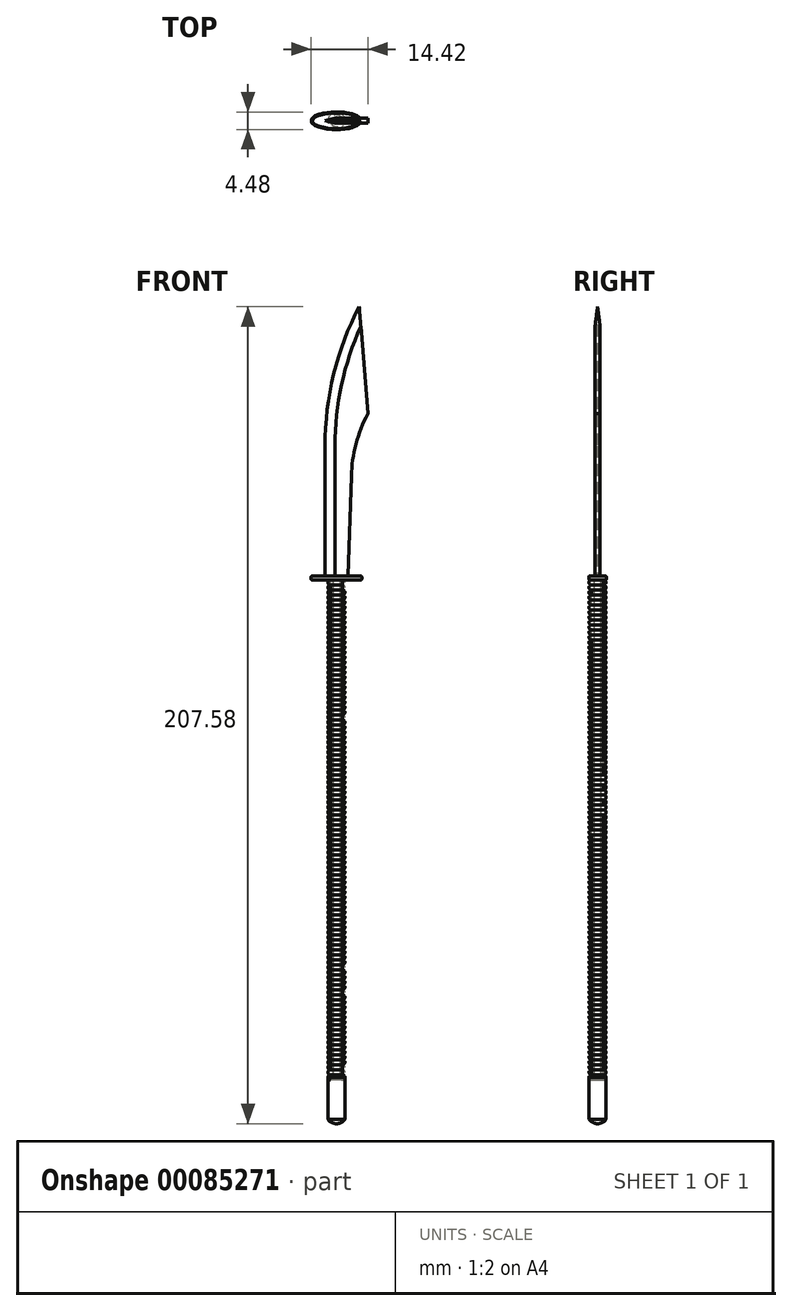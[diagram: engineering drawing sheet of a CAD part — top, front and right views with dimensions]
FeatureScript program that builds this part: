
annotation { "Feature Type Name" : "Feature", "Feature Type Description" : "" }
export const myFeature = defineFeature(function(context is Context, id is Id, definition is map)
    precondition{}
    {
        {
            var Q0;
            Q0=qCreatedBy(makeId("Right.planeOp"),FACE);
            var sketch = newSketch(context, id + "F0", { "sketchPlane" : qUnion([Q0])});
            skLineSegment(sketch, "E0", {"start": v(0, 0) * mm, "end": v(0, -127) * mm});
            skLineSegment(sketch, "E1", {"start": v(0, 0) * mm, "end": v(-1.52, 0) * mm});
            skLineSegment(sketch, "E2", {"start": v(-1.52, 0) * mm, "end": v(-1.52, -127) * mm});
            skLineSegment(sketch, "E3", {"start": v(0, -127) * mm, "end": v(-1.52, -127) * mm});
            skSolve(sketch);
        }
        {
            var Q0;
            Q0 = qSketchRegion(id + "F0", true);
            var Q1;
            Q1=sQuery(id+"F0.wireOp",EDGE,"E0");
            revolve(context, id + "F1", {"entities" : qUnion([Q0]), "axis" : qUnion([Q1]), "revolveType" : RevolveType.FULL});
        }
        {
            var Q0;
            Q0=qCreatedBy(makeId("Right.planeOp"),FACE);
            var sketch = newSketch(context, id + "F2", { "sketchPlane" : qUnion([Q0])});
            skLineSegment(sketch, "E4", {"start": v(-1.52, -127) * mm, "end": v(-1.52, 0) * mm});
            skCircle(sketch, "E5", {"center": v(-1.52, -0.63) * mm, "radius": 0.64 * mm});
            skCircle(sketch, "E6.1.0.0", {"center": v(-1.52, -1.9) * mm, "radius": 0.64 * mm});
            skCircle(sketch, "E6.2.0.0", {"center": v(-1.52, -3.17) * mm, "radius": 0.64 * mm});
            skCircle(sketch, "E6.3.0.0", {"center": v(-1.52, -4.44) * mm, "radius": 0.64 * mm});
            skCircle(sketch, "E6.4.0.0", {"center": v(-1.52, -5.71) * mm, "radius": 0.64 * mm});
            skCircle(sketch, "E6.5.0.0", {"center": v(-1.52, -6.98) * mm, "radius": 0.64 * mm});
            skCircle(sketch, "E6.6.0.0", {"center": v(-1.52, -8.25) * mm, "radius": 0.64 * mm});
            skCircle(sketch, "E6.7.0.0", {"center": v(-1.52, -9.52) * mm, "radius": 0.64 * mm});
            skCircle(sketch, "E6.8.0.0", {"center": v(-1.52, -10.8) * mm, "radius": 0.64 * mm});
            skCircle(sketch, "E6.9.0.0", {"center": v(-1.52, -12.06) * mm, "radius": 0.64 * mm});
            skCircle(sketch, "E6.10.0.0", {"center": v(-1.52, -13.33) * mm, "radius": 0.64 * mm});
            skCircle(sketch, "E6.11.0.0", {"center": v(-1.52, -14.6) * mm, "radius": 0.64 * mm});
            skCircle(sketch, "E6.12.0.0", {"center": v(-1.52, -15.88) * mm, "radius": 0.64 * mm});
            skCircle(sketch, "E6.13.0.0", {"center": v(-1.52, -17.14) * mm, "radius": 0.64 * mm});
            skCircle(sketch, "E6.14.0.0", {"center": v(-1.52, -18.41) * mm, "radius": 0.64 * mm});
            skCircle(sketch, "E6.15.0.0", {"center": v(-1.52, -19.69) * mm, "radius": 0.64 * mm});
            skCircle(sketch, "E6.16.0.0", {"center": v(-1.52, -20.96) * mm, "radius": 0.64 * mm});
            skCircle(sketch, "E6.17.0.0", {"center": v(-1.52, -22.23) * mm, "radius": 0.64 * mm});
            skCircle(sketch, "E6.18.0.0", {"center": v(-1.52, -23.5) * mm, "radius": 0.64 * mm});
            skCircle(sketch, "E6.19.0.0", {"center": v(-1.52, -24.77) * mm, "radius": 0.64 * mm});
            skCircle(sketch, "E6.20.0.0", {"center": v(-1.52, -26.04) * mm, "radius": 0.64 * mm});
            skCircle(sketch, "E6.21.0.0", {"center": v(-1.52, -27.3) * mm, "radius": 0.64 * mm});
            skCircle(sketch, "E6.22.0.0", {"center": v(-1.52, -28.58) * mm, "radius": 0.64 * mm});
            skCircle(sketch, "E6.23.0.0", {"center": v(-1.52, -29.85) * mm, "radius": 0.64 * mm});
            skCircle(sketch, "E6.24.0.0", {"center": v(-1.52, -31.12) * mm, "radius": 0.64 * mm});
            skCircle(sketch, "E6.25.0.0", {"center": v(-1.52, -32.39) * mm, "radius": 0.64 * mm});
            skCircle(sketch, "E6.26.0.0", {"center": v(-1.52, -33.66) * mm, "radius": 0.64 * mm});
            skCircle(sketch, "E6.27.0.0", {"center": v(-1.52, -34.93) * mm, "radius": 0.64 * mm});
            skCircle(sketch, "E6.28.0.0", {"center": v(-1.52, -36.2) * mm, "radius": 0.64 * mm});
            skCircle(sketch, "E6.29.0.0", {"center": v(-1.52, -37.47) * mm, "radius": 0.64 * mm});
            skCircle(sketch, "E6.30.0.0", {"center": v(-1.52, -38.74) * mm, "radius": 0.64 * mm});
            skCircle(sketch, "E6.31.0.0", {"center": v(-1.52, -40) * mm, "radius": 0.64 * mm});
            skCircle(sketch, "E6.32.0.0", {"center": v(-1.52, -41.28) * mm, "radius": 0.64 * mm});
            skCircle(sketch, "E6.33.0.0", {"center": v(-1.52, -42.55) * mm, "radius": 0.64 * mm});
            skCircle(sketch, "E6.34.0.0", {"center": v(-1.52, -43.82) * mm, "radius": 0.64 * mm});
            skCircle(sketch, "E6.35.0.0", {"center": v(-1.52, -45.09) * mm, "radius": 0.64 * mm});
            skCircle(sketch, "E6.36.0.0", {"center": v(-1.52, -46.36) * mm, "radius": 0.64 * mm});
            skCircle(sketch, "E6.37.0.0", {"center": v(-1.52, -47.63) * mm, "radius": 0.64 * mm});
            skCircle(sketch, "E6.38.0.0", {"center": v(-1.52, -48.9) * mm, "radius": 0.64 * mm});
            skCircle(sketch, "E6.39.0.0", {"center": v(-1.52, -50.17) * mm, "radius": 0.64 * mm});
            skCircle(sketch, "E6.40.0.0", {"center": v(-1.52, -51.44) * mm, "radius": 0.64 * mm});
            skCircle(sketch, "E6.41.0.0", {"center": v(-1.52, -52.7) * mm, "radius": 0.64 * mm});
            skCircle(sketch, "E6.42.0.0", {"center": v(-1.52, -53.98) * mm, "radius": 0.64 * mm});
            skCircle(sketch, "E6.43.0.0", {"center": v(-1.52, -55.25) * mm, "radius": 0.64 * mm});
            skCircle(sketch, "E6.44.0.0", {"center": v(-1.52, -56.52) * mm, "radius": 0.64 * mm});
            skCircle(sketch, "E6.45.0.0", {"center": v(-1.52, -57.79) * mm, "radius": 0.64 * mm});
            skCircle(sketch, "E6.46.0.0", {"center": v(-1.52, -59.06) * mm, "radius": 0.64 * mm});
            skCircle(sketch, "E6.47.0.0", {"center": v(-1.52, -60.33) * mm, "radius": 0.64 * mm});
            skCircle(sketch, "E6.48.0.0", {"center": v(-1.52, -61.6) * mm, "radius": 0.64 * mm});
            skCircle(sketch, "E6.49.0.0", {"center": v(-1.52, -62.87) * mm, "radius": 0.64 * mm});
            skCircle(sketch, "E6.50.0.0", {"center": v(-1.52, -64.14) * mm, "radius": 0.64 * mm});
            skCircle(sketch, "E6.51.0.0", {"center": v(-1.52, -65.4) * mm, "radius": 0.64 * mm});
            skCircle(sketch, "E6.52.0.0", {"center": v(-1.52, -66.68) * mm, "radius": 0.64 * mm});
            skCircle(sketch, "E6.53.0.0", {"center": v(-1.52, -67.95) * mm, "radius": 0.64 * mm});
            skCircle(sketch, "E6.54.0.0", {"center": v(-1.52, -69.22) * mm, "radius": 0.64 * mm});
            skCircle(sketch, "E6.55.0.0", {"center": v(-1.52, -70.49) * mm, "radius": 0.64 * mm});
            skCircle(sketch, "E6.56.0.0", {"center": v(-1.52, -71.76) * mm, "radius": 0.64 * mm});
            skCircle(sketch, "E6.57.0.0", {"center": v(-1.52, -73.03) * mm, "radius": 0.64 * mm});
            skCircle(sketch, "E6.58.0.0", {"center": v(-1.52, -74.3) * mm, "radius": 0.64 * mm});
            skCircle(sketch, "E6.59.0.0", {"center": v(-1.52, -75.57) * mm, "radius": 0.64 * mm});
            skCircle(sketch, "E6.60.0.0", {"center": v(-1.52, -76.84) * mm, "radius": 0.64 * mm});
            skCircle(sketch, "E6.61.0.0", {"center": v(-1.52, -78.1) * mm, "radius": 0.64 * mm});
            skCircle(sketch, "E6.62.0.0", {"center": v(-1.52, -79.38) * mm, "radius": 0.64 * mm});
            skCircle(sketch, "E6.63.0.0", {"center": v(-1.52, -80.65) * mm, "radius": 0.64 * mm});
            skCircle(sketch, "E6.64.0.0", {"center": v(-1.52, -81.92) * mm, "radius": 0.64 * mm});
            skCircle(sketch, "E6.65.0.0", {"center": v(-1.52, -83.19) * mm, "radius": 0.64 * mm});
            skCircle(sketch, "E6.66.0.0", {"center": v(-1.52, -84.46) * mm, "radius": 0.64 * mm});
            skCircle(sketch, "E6.67.0.0", {"center": v(-1.52, -85.73) * mm, "radius": 0.64 * mm});
            skCircle(sketch, "E6.68.0.0", {"center": v(-1.52, -87) * mm, "radius": 0.64 * mm});
            skCircle(sketch, "E6.69.0.0", {"center": v(-1.52, -88.27) * mm, "radius": 0.64 * mm});
            skCircle(sketch, "E6.70.0.0", {"center": v(-1.52, -89.54) * mm, "radius": 0.64 * mm});
            skCircle(sketch, "E6.71.0.0", {"center": v(-1.52, -90.8) * mm, "radius": 0.64 * mm});
            skCircle(sketch, "E6.72.0.0", {"center": v(-1.52, -92.08) * mm, "radius": 0.64 * mm});
            skCircle(sketch, "E6.73.0.0", {"center": v(-1.52, -93.35) * mm, "radius": 0.64 * mm});
            skCircle(sketch, "E6.74.0.0", {"center": v(-1.52, -94.62) * mm, "radius": 0.64 * mm});
            skCircle(sketch, "E6.75.0.0", {"center": v(-1.52, -95.89) * mm, "radius": 0.64 * mm});
            skCircle(sketch, "E6.76.0.0", {"center": v(-1.52, -97.16) * mm, "radius": 0.64 * mm});
            skCircle(sketch, "E6.77.0.0", {"center": v(-1.52, -98.43) * mm, "radius": 0.64 * mm});
            skCircle(sketch, "E6.78.0.0", {"center": v(-1.52, -99.7) * mm, "radius": 0.64 * mm});
            skCircle(sketch, "E6.79.0.0", {"center": v(-1.52, -100.97) * mm, "radius": 0.64 * mm});
            skCircle(sketch, "E6.80.0.0", {"center": v(-1.52, -102.24) * mm, "radius": 0.64 * mm});
            skCircle(sketch, "E6.81.0.0", {"center": v(-1.52, -103.5) * mm, "radius": 0.64 * mm});
            skCircle(sketch, "E6.82.0.0", {"center": v(-1.52, -104.78) * mm, "radius": 0.64 * mm});
            skCircle(sketch, "E6.83.0.0", {"center": v(-1.52, -106.05) * mm, "radius": 0.64 * mm});
            skCircle(sketch, "E6.84.0.0", {"center": v(-1.52, -107.32) * mm, "radius": 0.64 * mm});
            skCircle(sketch, "E6.85.0.0", {"center": v(-1.52, -108.59) * mm, "radius": 0.64 * mm});
            skCircle(sketch, "E6.86.0.0", {"center": v(-1.52, -109.86) * mm, "radius": 0.64 * mm});
            skCircle(sketch, "E6.87.0.0", {"center": v(-1.52, -111.13) * mm, "radius": 0.64 * mm});
            skCircle(sketch, "E6.88.0.0", {"center": v(-1.52, -112.4) * mm, "radius": 0.64 * mm});
            skCircle(sketch, "E6.89.0.0", {"center": v(-1.52, -113.67) * mm, "radius": 0.64 * mm});
            skCircle(sketch, "E6.90.0.0", {"center": v(-1.52, -114.94) * mm, "radius": 0.64 * mm});
            skCircle(sketch, "E6.91.0.0", {"center": v(-1.52, -116.2) * mm, "radius": 0.64 * mm});
            skCircle(sketch, "E6.92.0.0", {"center": v(-1.52, -117.48) * mm, "radius": 0.64 * mm});
            skCircle(sketch, "E6.93.0.0", {"center": v(-1.52, -118.75) * mm, "radius": 0.64 * mm});
            skCircle(sketch, "E6.94.0.0", {"center": v(-1.52, -120.02) * mm, "radius": 0.64 * mm});
            skCircle(sketch, "E6.95.0.0", {"center": v(-1.52, -121.29) * mm, "radius": 0.64 * mm});
            skCircle(sketch, "E6.96.0.0", {"center": v(-1.52, -122.56) * mm, "radius": 0.64 * mm});
            skCircle(sketch, "E6.97.0.0", {"center": v(-1.52, -123.83) * mm, "radius": 0.64 * mm});
            skCircle(sketch, "E6.98.0.0", {"center": v(-1.52, -125.1) * mm, "radius": 0.64 * mm});
            skCircle(sketch, "E6.99.0.0", {"center": v(-1.52, -126.37) * mm, "radius": 0.64 * mm});
            skLineSegment(sketch, "E6.direction1", {"start": v(-1.52, -0.63) * mm, "end": v(-1.52, -1.9) * mm, "construction": true});
            skLineSegment(sketch, "E7", {"start": v(0, 0) * mm, "end": v(0, -126.88) * mm});
            skLineSegment(sketch, "E8", {"start": v(0, -126.88) * mm, "end": v(15.16, -117.8) * mm});
            skSolve(sketch);
        }
        {
            var Q0;
            Q0 = qSketchRegion(id + "F2", true);
            var Q1;
            Q1=sQuery(id+"F2.wireOp",EDGE,"E7");
            revolve(context, id + "F3", {"entities" : qUnion([Q0]), "axis" : qUnion([Q1]), "revolveType" : RevolveType.FULL});
        }
        {
            var Q0;
            Q0=makeQuery(id+"F1.opRevolve","SWEPT_FACE",FACE,{"disambiguationData":[OSD([sQuery(id+"F0.wireOp",EDGE,"E1")])]});
            var sketch = newSketch(context, id + "F4", { "sketchPlane" : qUnion([Q0])});
            skPoint(sketch, "E9", {"position": v(0, -2.24) * mm});
            skPoint(sketch, "E10", {"position": v(0, 2.24) * mm});
            skEllipse(sketch, "E11", {"center": v(0, 0) * mm, "majorRadius": 2.24 * mm, "minorRadius": 6.44 * mm, "majorAxis": v(0, -1)});
            skLineSegment(sketch, "E12", {"start": v(6.44, 0) * mm, "end": v(-6.44, 0) * mm});
            skSolve(sketch);
        }
        {
            var Q0;
            Q0 = qSketchRegion(id + "F4", true);
            extrude(context, id + "F5", {"entities" : qUnion([Q0]), "depth" : 1.02 * mm});
        }
        {
            var Q0;
            Q0=makeQuery(id+"F5.opExtrude","CAP_EDGE",EDGE,{"disambiguationData":[OSD([sQuery(id+"F4.wireOp",EDGE,"E11")])],"isStart":false});
            var Q1;
            Q1=makeQuery(id+"F5.opExtrude","CAP_EDGE",EDGE,{"disambiguationData":[OSD([sQuery(id+"F4.wireOp",EDGE,"E11")])],"isStart":true});
            fillet(context, id + "F6", {"entities" : qUnion([Q0, Q1]), "radius" : 0.25 * mm, "tangentPropagation" : true, "allowEdgeOverflow" : false});
        }
        {
            var Q0;
            Q0=qCreatedBy(makeId("Front.planeOp"),FACE);
            var sketch = newSketch(context, id + "F7", { "sketchPlane" : qUnion([Q0])});
            skLineSegment(sketch, "E13.0", {"start": v(6.44, 0) * mm, "end": v(-6.44, 0) * mm});
            skLineSegment(sketch, "E14.top", {"start": v(6.44, 1.02) * mm, "end": v(-6.44, 1.02) * mm});
            skLineSegment(sketch, "E14.left", {"start": v(6.44, 0) * mm, "end": v(6.44, 1.02) * mm});
            skLineSegment(sketch, "E14.right", {"start": v(-6.44, 0) * mm, "end": v(-6.44, 1.02) * mm});
            skPoint(sketch, "E15", {"position": v(2.88, 1.02) * mm});
            skPoint(sketch, "E16", {"position": v(-2.88, 1.02) * mm});
            skLineSegment(sketch, "E17", {"start": v(2.88, 1.02) * mm, "end": v(3.77, 26.4) * mm});
            skLineSegment(sketch, "E18", {"start": v(-2.88, 1.02) * mm, "end": v(-2.88, 34.04) * mm});
            skArc(sketch, "E19", {"start": v(5.78, 69.43) * mm, "mid": v(-0.69, 52.26) * mm, "end": v(-2.88, 34.04) * mm});
            skArc(sketch, "E20", {"start": v(7.98, 42.21) * mm, "mid": v(4.98, 34.54) * mm, "end": v(3.77, 26.4) * mm});
            skLineSegment(sketch, "E21", {"start": v(7.98, 42.21) * mm, "end": v(5.78, 69.43) * mm});
            skSolve(sketch);
        }
        {
            var Q0;
            {var subQ0=sQuery(id+"F7.wireOp",EDGE,"E17");Q0=makeQuery(id+"F7.imprint","IMPRINT",FACE,{"disambiguationData":[TD([[makeQuery(id+"F7.imprint","IMPRINT",EDGE,{"derivedFrom":subQ0}),1.0]])]});}
            extrude(context, id + "F8", {"entities" : qUnion([Q0]), "endBound" : BoundingType.SYMMETRIC, "depth" : 1.27 * mm});
        }
        {
            var Q0;
            Q0=makeQuery(id+"F8.opExtrude","CAP_EDGE",EDGE,{"disambiguationData":[OSD([sQuery(id+"F7.wireOp",EDGE,"E19")])],"isStart":true});
            var Q1;
            Q1=makeQuery(id+"F8.opExtrude","CAP_EDGE",EDGE,{"disambiguationData":[OSD([sQuery(id+"F7.wireOp",EDGE,"E18")])],"isStart":true});
            var Q2;
            Q2=makeQuery(id+"F8.opExtrude","CAP_EDGE",EDGE,{"disambiguationData":[OSD([sQuery(id+"F7.wireOp",EDGE,"E19")])],"isStart":false});
            var Q3;
            Q3=makeQuery(id+"F8.opExtrude","CAP_EDGE",EDGE,{"disambiguationData":[OSD([sQuery(id+"F7.wireOp",EDGE,"E18")])],"isStart":false});
            chamfer(context, id + "F9", {"entities" : qUnion([Q0, Q1, Q2, Q3]), "chamferType" : ChamferType.TWO_OFFSETS, "width1" : 0.64 * mm, "oppositeDirection" : false, "width2" : 2.54 * mm, "tangentPropagation" : true});
        }
        {
            var Q0;
            Q0=qCreatedBy(makeId("Front.planeOp"),FACE);
            var sketch = newSketch(context, id + "F10", { "sketchPlane" : qUnion([Q0])});
            skLineSegment(sketch, "E22.0", {"start": v(-1.52, -127) * mm, "end": v(1.52, -127) * mm});
            skLineSegment(sketch, "E23", {"start": v(-1.52, -125.73) * mm, "end": v(1.52, -125.73) * mm});
            skArc(sketch, "E24", {"start": v(-1.52, -127) * mm, "mid": v(-0.89, -126.37) * mm, "end": v(-1.52, -125.73) * mm});
            skArc(sketch, "E25", {"start": v(1.52, -125.73) * mm, "mid": v(0.89, -126.37) * mm, "end": v(1.52, -127) * mm});
            skPoint(sketch, "E26.orphan", {"position": v(3.21, -126.37) * mm});
            skPoint(sketch, "E27.orphan", {"position": v(-2.81, -126.37) * mm});
            skCircle(sketch, "E28", {"center": v(-1.52, -126.37) * mm, "radius": 0.63 * mm});
            skCircle(sketch, "E29", {"center": v(1.52, -126.37) * mm, "radius": 0.63 * mm});
            skLineSegment(sketch, "E30", {"start": v(-1.52, -126.37) * mm, "end": v(-2.16, -126.37) * mm});
            skLineSegment(sketch, "E31", {"start": v(1.52, -126.37) * mm, "end": v(2.16, -126.37) * mm});
            skLineSegment(sketch, "E32", {"start": v(-2.16, -126.37) * mm, "end": v(-2.16, -127) * mm});
            skLineSegment(sketch, "E33", {"start": v(2.16, -126.37) * mm, "end": v(2.16, -127) * mm});
            skLineSegment(sketch, "E34", {"start": v(-1.52, -127) * mm, "end": v(-2.16, -127) * mm});
            skLineSegment(sketch, "E35", {"start": v(1.52, -127) * mm, "end": v(2.16, -127) * mm});
            skLineSegment(sketch, "E36", {"start": v(2.16, -127) * mm, "end": v(2.16, -137.1) * mm});
            skLineSegment(sketch, "E37", {"start": v(0, -127) * mm, "end": v(0, -129.18) * mm});
            skPoint(sketch, "E37.endSnap0", {"position": v(0, -127) * mm});
            skLineSegment(sketch, "E38.MirrorCS", {"start": v(-2.16, -127) * mm, "end": v(-2.16, -137.1) * mm});
            skArc(sketch, "E39", {"start": v(-2.16, -137.1) * mm, "mid": v(0, -138.15) * mm, "end": v(2.16, -137.1) * mm});
            skLineSegment(sketch, "E40", {"start": v(0, -129.18) * mm, "end": v(0, -138.15) * mm});
            skSolve(sketch);
        }
        {
            var Q0;
            {var subQ2=sQuery(id+"F10.wireOp",EDGE,"E35");Q0=makeQuery(id+"F10.imprint","IMPRINT",FACE,{"disambiguationData":[TD([[makeQuery(id+"F10.imprint","IMPRINT",EDGE,{"derivedFrom":subQ2}),-1.0]])]});}
            var Q1;
            {var subQ2=sQuery(id+"F10.wireOp",EDGE,"E33");Q1=makeQuery(id+"F10.imprint","IMPRINT",FACE,{"disambiguationData":[TD([[makeQuery(id+"F10.imprint","IMPRINT",EDGE,{"derivedFrom":subQ2}),-1.0]])]});}
            var Q2;
            Q2=sQuery(id+"F10.wireOp",EDGE,"E40");
            revolve(context, id + "F11", {"entities" : qUnion([Q0, Q1]), "axis" : qUnion([Q2]), "revolveType" : RevolveType.FULL});
        }
    });
